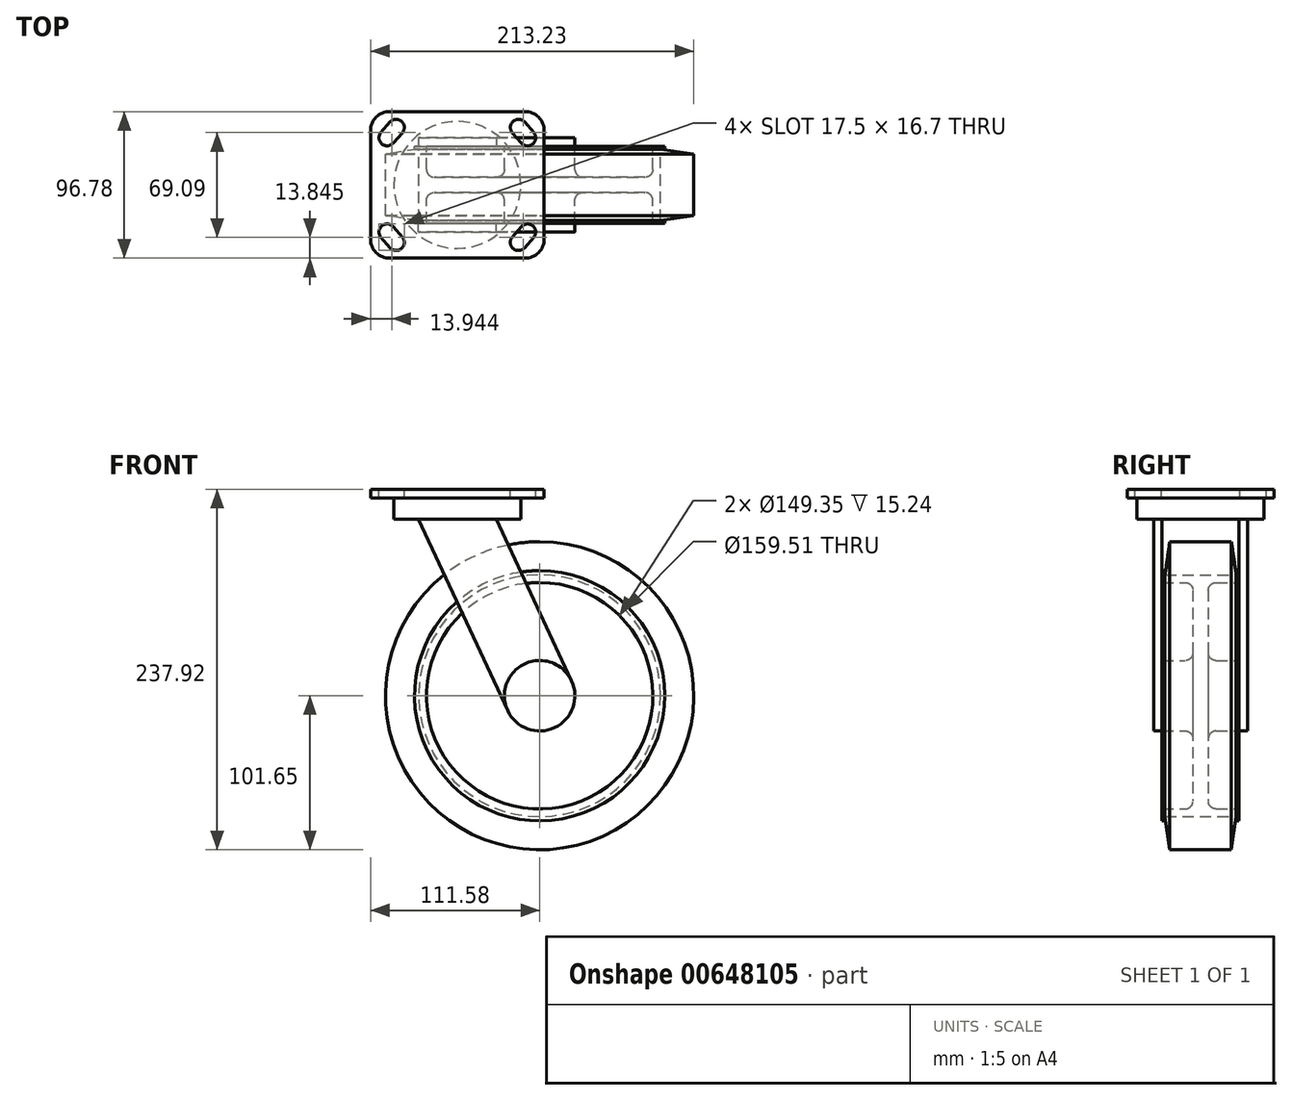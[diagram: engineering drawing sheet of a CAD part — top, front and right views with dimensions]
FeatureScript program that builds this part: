
annotation { "Feature Type Name" : "Feature", "Feature Type Description" : "" }
export const myFeature = defineFeature(function(context is Context, id is Id, definition is map)
    precondition{}
    {
        {
            var Q0;
            Q0=qCreatedBy(makeId("Right.planeOp"),FACE);
            var sketch = newSketch(context, id + "F0", { "sketchPlane" : qUnion([Q0])});
            skLineSegment(sketch, "E0", {"start": v(25.4, 0) * mm, "end": v(25.4, 23.24) * mm});
            skLineSegment(sketch, "E1", {"start": v(25.4, 23.24) * mm, "end": v(5.08, 23.24) * mm});
            skLineSegment(sketch, "E2", {"start": v(5.08, 23.24) * mm, "end": v(5.08, 74.68) * mm});
            skLineSegment(sketch, "E3", {"start": v(5.08, 74.68) * mm, "end": v(25.4, 74.68) * mm});
            skLineSegment(sketch, "E4", {"start": v(25.4, 74.68) * mm, "end": v(25.4, 82.55) * mm});
            skLineSegment(sketch, "E5", {"start": v(25.4, 82.55) * mm, "end": v(23.5, 82.55) * mm});
            skLineSegment(sketch, "E6", {"start": v(23.5, 82.55) * mm, "end": v(23.5, 79.76) * mm});
            skLineSegment(sketch, "E7", {"start": v(23.5, 79.76) * mm, "end": v(0, 79.76) * mm});
            skLineSegment(sketch, "E8.MirrorCS", {"start": v(-25.4, 82.55) * mm, "end": v(-23.5, 82.55) * mm});
            skLineSegment(sketch, "E9.MirrorCS", {"start": v(-23.5, 82.55) * mm, "end": v(-23.5, 79.76) * mm});
            skLineSegment(sketch, "E10.MirrorCS", {"start": v(-25.4, 23.24) * mm, "end": v(-5.08, 23.24) * mm});
            skLineSegment(sketch, "E11.MirrorCS", {"start": v(-5.08, 74.68) * mm, "end": v(-25.4, 74.68) * mm});
            skLineSegment(sketch, "E12.MirrorCS", {"start": v(-25.4, 74.68) * mm, "end": v(-25.4, 82.55) * mm});
            skLineSegment(sketch, "E13.MirrorCS", {"start": v(-23.5, 79.76) * mm, "end": v(0, 79.76) * mm});
            skLineSegment(sketch, "E14.MirrorCS", {"start": v(-5.08, 23.24) * mm, "end": v(-5.08, 74.68) * mm});
            skLineSegment(sketch, "E15.MirrorCS", {"start": v(-25.4, 0) * mm, "end": v(-25.4, 23.24) * mm});
            skLineSegment(sketch, "E16", {"start": v(25.4, 0) * mm, "end": v(0, 0) * mm});
            skLineSegment(sketch, "E17", {"start": v(0, 0) * mm, "end": v(-25.4, 0) * mm});
            skSolve(sketch);
        }
        {
            var Q0;
            Q0 = qSketchRegion(id + "F0", true);
            var Q1;
            Q1=sQuery(id+"F0.wireOp",EDGE,"E0");
            var Q2;
            Q2=sQuery(id+"F0.wireOp",EDGE,"E1");
            var Q3;
            Q3=sQuery(id+"F0.wireOp",EDGE,"E2");
            var Q4;
            Q4=sQuery(id+"F0.wireOp",EDGE,"E3");
            var Q5;
            Q5=sQuery(id+"F0.wireOp",EDGE,"E4");
            var Q6;
            Q6=sQuery(id+"F0.wireOp",EDGE,"E5");
            var Q7;
            Q7=sQuery(id+"F0.wireOp",EDGE,"E6");
            var Q8;
            Q8=sQuery(id+"F0.wireOp",EDGE,"E7");
            var Q9;
            Q9=sQuery(id+"F0.wireOp",EDGE,"E8.MirrorCS");
            var Q10;
            Q10=sQuery(id+"F0.wireOp",EDGE,"E9.MirrorCS");
            var Q11;
            Q11=sQuery(id+"F0.wireOp",EDGE,"E10.MirrorCS");
            var Q12;
            Q12=sQuery(id+"F0.wireOp",EDGE,"E11.MirrorCS");
            var Q13;
            Q13=sQuery(id+"F0.wireOp",EDGE,"E12.MirrorCS");
            var Q14;
            Q14=sQuery(id+"F0.wireOp",EDGE,"E13.MirrorCS");
            var Q15;
            Q15=sQuery(id+"F0.wireOp",EDGE,"E14.MirrorCS");
            var Q16;
            Q16=sQuery(id+"F0.wireOp",EDGE,"E15.MirrorCS");
            var Q17;
            Q17=sQuery(id+"F0.wireOp",EDGE,"E17");
            revolve(context, id + "F1", {"entities" : qUnion([Q0]), "surfaceEntities" : qUnion([Q1, Q2, Q3, Q4, Q5, Q6, Q7, Q8, Q9, Q10, Q11, Q12, Q13, Q14, Q15, Q16]), "axis" : qUnion([Q17]), "revolveType" : RevolveType.FULL});
        }
        {
            var Q0;
            Q0=makeQuery(id+"F1.opRevolve","SWEPT_FACE",FACE,{"disambiguationData":[OSD([sQuery(id+"F0.wireOp",EDGE,"E2")])]});
            var Q1;
            Q1=makeQuery(id+"F1.opRevolve","SWEPT_FACE",FACE,{"disambiguationData":[OSD([sQuery(id+"F0.wireOp",EDGE,"E14.MirrorCS")])]});
            fillet(context, id + "F2", {"entities" : qUnion([Q0, Q1]), "radius" : 5.08 * mm, "tangentPropagation" : true, "allowEdgeOverflow" : false});
        }
        {
            var Q0;
            Q0=qCreatedBy(makeId("Right.planeOp"),FACE);
            var sketch = newSketch(context, id + "F3", { "sketchPlane" : qUnion([Q0])});
            skLineSegment(sketch, "E18", {"start": v(23.5, -79.76) * mm, "end": v(-23.5, -79.76) * mm});
            skLineSegment(sketch, "E19", {"start": v(23.5, -79.76) * mm, "end": v(20.32, -101.65) * mm});
            skLineSegment(sketch, "E20", {"start": v(20.32, -101.65) * mm, "end": v(-20.32, -101.65) * mm});
            skLineSegment(sketch, "E21", {"start": v(-20.32, -101.65) * mm, "end": v(-23.5, -79.76) * mm});
            skLineSegment(sketch, "E22", {"start": v(0, -79.76) * mm, "end": v(0, -57.04) * mm, "construction": true});
            skLineSegment(sketch, "E23", {"start": v(0, 0) * mm, "end": v(-31, 0) * mm, "construction": true});
            skSolve(sketch);
        }
        {
            var Q0;
            Q0 = qSketchRegion(id + "F3", true);
            var Q1;
            Q1=sQuery(id+"F3.wireOp",EDGE,"E23");
            revolve(context, id + "F4", {"entities" : qUnion([Q0]), "axis" : qUnion([Q1]), "revolveType" : RevolveType.FULL});
        }
        {
            var Q0;
            Q0=makeQuery(id+"F1.opRevolve","SWEPT_FACE",FACE,{"disambiguationData":[OSD([sQuery(id+"F0.wireOp",EDGE,"E15.MirrorCS")])]});
            var sketch = newSketch(context, id + "F5", { "sketchPlane" : qUnion([Q0])});
            skArc(sketch, "E24.0", {"start": v(-21.06, -9.82) * mm, "mid": v(9.82, -21.06) * mm, "end": v(21.06, 9.82) * mm});
            skLineSegment(sketch, "E25", {"start": v(-21.06, -9.82) * mm, "end": v(-79.95, 116.46) * mm});
            skLineSegment(sketch, "E26", {"start": v(-79.95, 116.46) * mm, "end": v(-28.66, 116.46) * mm});
            skLineSegment(sketch, "E27", {"start": v(-28.66, 116.46) * mm, "end": v(21.06, 9.82) * mm});
            skSolve(sketch);
        }
        {
            var Q0;
            Q0 = qSketchRegion(id + "F5", true);
            extrude(context, id + "F6", {"entities" : qUnion([Q0]), "depth" : 5.6 * mm, "offsetDistance" : 25.4 * mm});
        }
        {
            var Q0;
            Q0=makeQuery(id+"F6.opExtrude","SWEPT_BODY",BODY,{"disambiguationData":[OSD([sQuery(id+"F5.wireOp",EDGE,"E24.0"),sQuery(id+"F5.wireOp",EDGE,"E25"),sQuery(id+"F5.wireOp",EDGE,"E26"),sQuery(id+"F5.wireOp",EDGE,"E27")])]});
            var Q1;
            Q1=qCreatedBy(makeId("Front.planeOp"),FACE);
            mirror(context, id + "F7", {"entities" : qUnion([Q0]), "mirrorPlane" : qUnion([Q1])});
        }
        {
            var Q0;
            Q0=makeQuery(id+"F7.opPattern","COPY",FACE,{"derivedFrom":makeQuery(id+"F6.opExtrude","SWEPT_FACE",FACE,{"disambiguationData":[OSD([sQuery(id+"F5.wireOp",EDGE,"E26")])]}),"instanceName":"1"});
            var sketch = newSketch(context, id + "F8", { "sketchPlane" : qUnion([Q0])});
            skCircle(sketch, "E28", {"center": v(-54.3, 0) * mm, "radius": 41.91 * mm});
            skPoint(sketch, "E28.centerSnap0", {"position": v(-54.3, 25.4) * mm});
            skSolve(sketch);
        }
        {
            var Q0;
            Q0 = qSketchRegion(id + "F8", true);
            extrude(context, id + "F9", {"entities" : qUnion([Q0]), "operationType" : NewBodyOperationType.ADD, "depth" : 13.97 * mm, "offsetDistance" : 25.4 * mm});
        }
        {
            var Q0;
            Q0=makeQuery(id+"F9.opExtrude","CAP_FACE",FACE,{"disambiguationData":[OSD([sQuery(id+"F8.wireOp",EDGE,"E28")])],"isStart":false});
            var sketch = newSketch(context, id + "F10", { "sketchPlane" : qUnion([Q0])});
            skLineSegment(sketch, "E29.bottom", {"start": v(-9.73, -48.39) * mm, "end": v(-98.88, -48.39) * mm});
            skLineSegment(sketch, "E29.top", {"start": v(-9.73, 48.39) * mm, "end": v(-98.88, 48.39) * mm});
            skLineSegment(sketch, "E29.left", {"start": v(2.97, -35.69) * mm, "end": v(2.97, 35.69) * mm});
            skLineSegment(sketch, "E29.right", {"start": v(-111.58, -35.69) * mm, "end": v(-111.58, 35.69) * mm});
            skPoint(sketch, "E29.middle", {"position": v(-54.3, 0) * mm});
            skPoint(sketch, "E30.visualSharp", {"position": v(-111.58, 48.39) * mm});
            skArc(sketch, "E30.filletArc", {"start": v(-98.88, 48.39) * mm, "mid": v(-107.86, 44.67) * mm, "end": v(-111.58, 35.69) * mm});
            skPoint(sketch, "E31.visualSharp", {"position": v(-111.58, -48.39) * mm});
            skArc(sketch, "E31.filletArc", {"start": v(-111.58, -35.69) * mm, "mid": v(-107.86, -44.67) * mm, "end": v(-98.88, -48.39) * mm});
            skPoint(sketch, "E32.visualSharp", {"position": v(2.97, -48.39) * mm});
            skArc(sketch, "E32.filletArc", {"start": v(-9.73, -48.39) * mm, "mid": v(-0.75, -44.67) * mm, "end": v(2.97, -35.69) * mm});
            skPoint(sketch, "E33.visualSharp", {"position": v(2.97, 48.39) * mm});
            skArc(sketch, "E33.filletArc", {"start": v(2.97, 35.69) * mm, "mid": v(-0.75, 44.67) * mm, "end": v(-9.73, 48.39) * mm});
            skSolve(sketch);
        }
        {
            var Q0;
            Q0 = qSketchRegion(id + "F10", true);
            extrude(context, id + "F11", {"entities" : qUnion([Q0]), "operationType" : NewBodyOperationType.ADD, "depth" : 5.84 * mm, "offsetDistance" : 25.4 * mm});
        }
        {
            var Q0;
            Q0=makeQuery(id+"F11.opExtrude","CAP_FACE",FACE,{"disambiguationData":[OSD([sQuery(id+"F10.wireOp",EDGE,"E29.bottom"),sQuery(id+"F10.wireOp",EDGE,"E29.top"),sQuery(id+"F10.wireOp",EDGE,"E29.left"),sQuery(id+"F10.wireOp",EDGE,"E29.right"),sQuery(id+"F10.wireOp",EDGE,"E30.filletArc"),sQuery(id+"F10.wireOp",EDGE,"E31.filletArc"),sQuery(id+"F10.wireOp",EDGE,"E32.filletArc"),sQuery(id+"F10.wireOp",EDGE,"E33.filletArc")])],"isStart":false});
            var sketch = newSketch(context, id + "F12", { "sketchPlane" : qUnion([Q0])});
            skLineSegment(sketch, "E34", {"start": v(-100.66, 31.12) * mm, "end": v(-94.61, 37.97) * mm, "construction": true});
            skArc(sketch, "E35.0.startCap", {"start": v(-96.66, 27.59) * mm, "mid": v(-104.19, 27.12) * mm, "end": v(-104.66, 34.65) * mm});
            skArc(sketch, "E35.0.endCap", {"start": v(-98.61, 41.5) * mm, "mid": v(-91.08, 41.97) * mm, "end": v(-90.61, 34.44) * mm});
            skLineSegment(sketch, "E35.0.left", {"start": v(-104.66, 34.65) * mm, "end": v(-98.61, 41.5) * mm});
            skLineSegment(sketch, "E35.0.right", {"start": v(-96.66, 27.59) * mm, "end": v(-90.61, 34.44) * mm});
            skLineSegment(sketch, "E36", {"start": v(-54.3, 48.39) * mm, "end": v(-54.3, -48.39) * mm, "construction": true});
            skLineSegment(sketch, "E37", {"start": v(-111.58, 0) * mm, "end": v(2.97, 0) * mm, "construction": true});
            skArc(sketch, "E38.MirrorCS", {"start": v(-104.66, 34.65) * mm, "mid": v(-104.19, 27.12) * mm, "end": v(-96.66, 27.59) * mm});
            skArc(sketch, "E39.MirrorCS", {"start": v(-90.61, 34.44) * mm, "mid": v(-91.08, 41.97) * mm, "end": v(-98.61, 41.5) * mm});
            skArc(sketch, "E40.MirrorCS", {"start": v(-11.95, 27.59) * mm, "mid": v(-4.42, 27.12) * mm, "end": v(-3.95, 34.65) * mm});
            skArc(sketch, "E41.MirrorCS", {"start": v(-10, 41.5) * mm, "mid": v(-17.53, 41.97) * mm, "end": v(-18, 34.44) * mm});
            skLineSegment(sketch, "E42.MirrorCS", {"start": v(-11.95, 27.59) * mm, "end": v(-18, 34.44) * mm});
            skLineSegment(sketch, "E43.MirrorCS", {"start": v(-3.95, 34.65) * mm, "end": v(-10, 41.5) * mm});
            skArc(sketch, "E44.MirrorCS", {"start": v(-3.95, 34.65) * mm, "mid": v(-4.42, 27.12) * mm, "end": v(-11.95, 27.59) * mm});
            skLineSegment(sketch, "E45.MirrorCS", {"start": v(-7.95, 31.12) * mm, "end": v(-14, 37.97) * mm, "construction": true});
            skArc(sketch, "E46.MirrorCS", {"start": v(-18, 34.44) * mm, "mid": v(-17.53, 41.97) * mm, "end": v(-10, 41.5) * mm});
            skLineSegment(sketch, "E47.MirrorCS", {"start": v(-11.95, -27.59) * mm, "end": v(-18, -34.44) * mm});
            skArc(sketch, "E48.MirrorCS", {"start": v(-96.66, -27.59) * mm, "mid": v(-104.19, -27.12) * mm, "end": v(-104.66, -34.65) * mm});
            skArc(sketch, "E49.MirrorCS", {"start": v(-10, -41.5) * mm, "mid": v(-17.53, -41.97) * mm, "end": v(-18, -34.44) * mm});
            skArc(sketch, "E50.MirrorCS", {"start": v(-98.61, -41.5) * mm, "mid": v(-91.08, -41.97) * mm, "end": v(-90.61, -34.44) * mm});
            skLineSegment(sketch, "E51.MirrorCS", {"start": v(-3.95, -34.65) * mm, "end": v(-10, -41.5) * mm});
            skArc(sketch, "E52.MirrorCS", {"start": v(-11.95, -27.59) * mm, "mid": v(-4.42, -27.12) * mm, "end": v(-3.95, -34.65) * mm});
            skLineSegment(sketch, "E53.MirrorCS", {"start": v(-104.66, -34.65) * mm, "end": v(-98.61, -41.5) * mm});
            skLineSegment(sketch, "E54.MirrorCS", {"start": v(-96.66, -27.59) * mm, "end": v(-90.61, -34.44) * mm});
            skLineSegment(sketch, "E55.MirrorCS", {"start": v(-7.95, -31.12) * mm, "end": v(-14, -37.97) * mm, "construction": true});
            skLineSegment(sketch, "E56.MirrorCS", {"start": v(-100.66, -31.12) * mm, "end": v(-94.61, -37.97) * mm, "construction": true});
            skArc(sketch, "E57.MirrorCS", {"start": v(-3.95, -34.65) * mm, "mid": v(-4.42, -27.12) * mm, "end": v(-11.95, -27.59) * mm});
            skArc(sketch, "E58.MirrorCS", {"start": v(-104.66, -34.65) * mm, "mid": v(-104.19, -27.12) * mm, "end": v(-96.66, -27.59) * mm});
            skArc(sketch, "E59.MirrorCS", {"start": v(-90.61, -34.44) * mm, "mid": v(-91.08, -41.97) * mm, "end": v(-98.61, -41.5) * mm});
            skArc(sketch, "E60.MirrorCS", {"start": v(-18, -34.44) * mm, "mid": v(-17.53, -41.97) * mm, "end": v(-10, -41.5) * mm});
            skSolve(sketch);
        }
        {
            var Q0;
            Q0 = qSketchRegion(id + "F12", true);
            var Q1;
            Q1=makeQuery(id+"F11.opExtrude","CAP_FACE",FACE,{"disambiguationData":[OSD([sQuery(id+"F10.wireOp",EDGE,"E29.bottom"),sQuery(id+"F10.wireOp",EDGE,"E29.top"),sQuery(id+"F10.wireOp",EDGE,"E29.left"),sQuery(id+"F10.wireOp",EDGE,"E29.right"),sQuery(id+"F10.wireOp",EDGE,"E30.filletArc"),sQuery(id+"F10.wireOp",EDGE,"E31.filletArc"),sQuery(id+"F10.wireOp",EDGE,"E32.filletArc"),sQuery(id+"F10.wireOp",EDGE,"E33.filletArc")])],"isStart":true});
            extrude(context, id + "F13", {"entities" : qUnion([Q0]), "operationType" : NewBodyOperationType.REMOVE, "endBound" : BoundingType.UP_TO_SURFACE, "oppositeDirection" : true, "depth" : 25.4 * mm, "endBoundEntityFace" : qUnion([Q1]), "offsetDistance" : 25.4 * mm});
        }
    });
